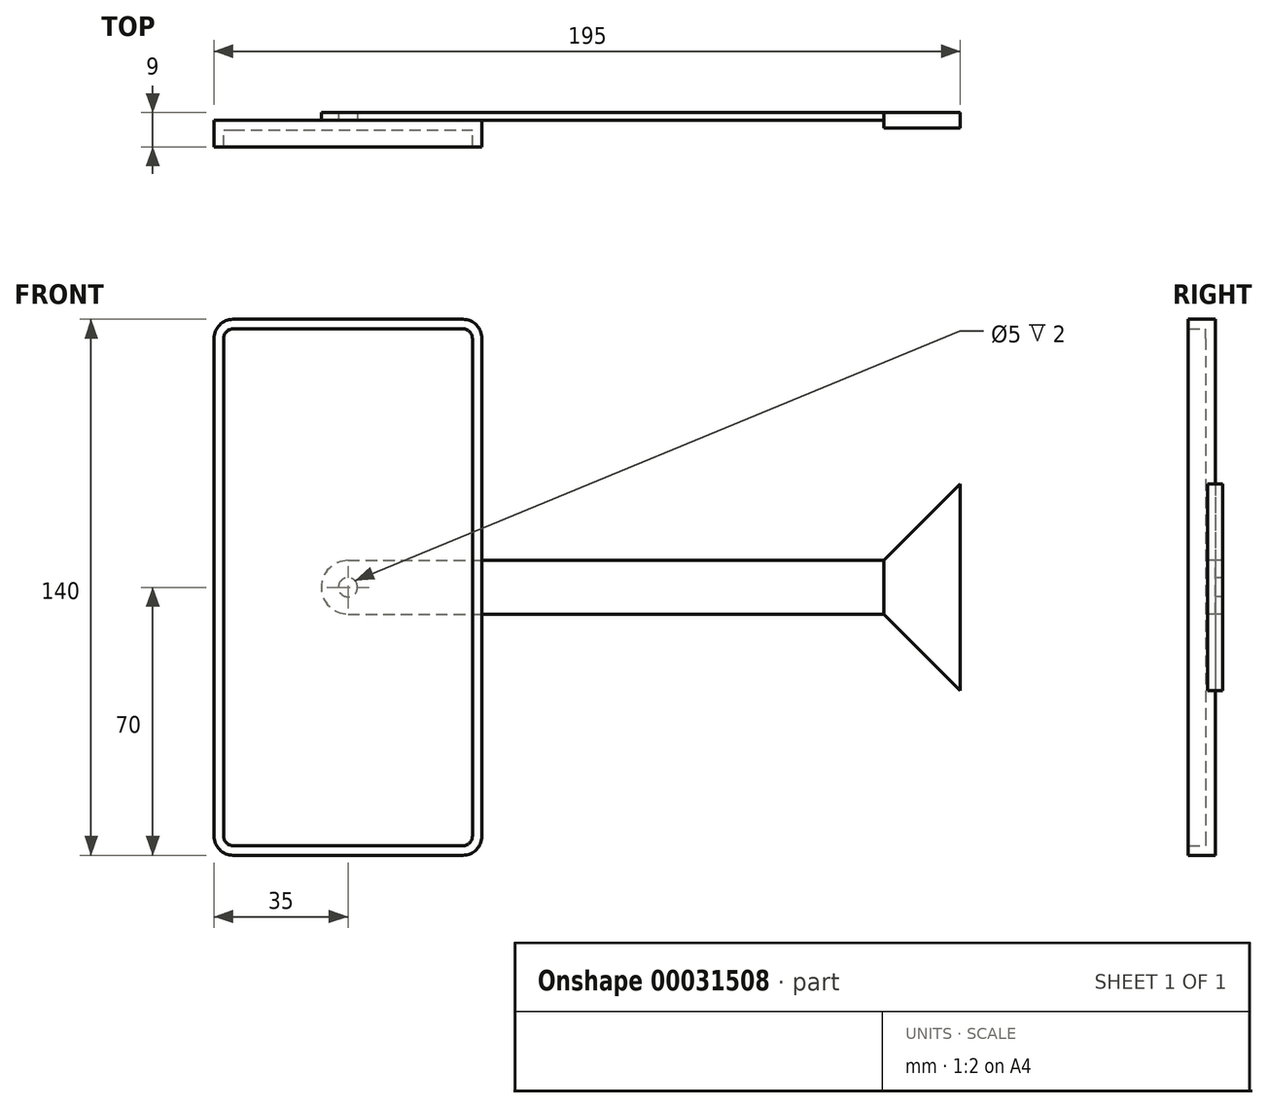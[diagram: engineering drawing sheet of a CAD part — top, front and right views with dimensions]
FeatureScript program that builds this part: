
annotation { "Feature Type Name" : "Feature", "Feature Type Description" : "" }
export const myFeature = defineFeature(function(context is Context, id is Id, definition is map)
    precondition{}
    {
        {
            var Q0;
            Q0=qCreatedBy(makeId("Front.planeOp"),FACE);
            var sketch = newSketch(context, id + "F0", { "sketchPlane" : qUnion([Q0])});
            skLineSegment(sketch, "E0.bottom", {"start": v(-35, 70) * mm, "end": v(35, 70) * mm});
            skLineSegment(sketch, "E0.top", {"start": v(-35, -70) * mm, "end": v(35, -70) * mm});
            skLineSegment(sketch, "E0.left", {"start": v(-35, 70) * mm, "end": v(-35, -70) * mm});
            skLineSegment(sketch, "E0.right", {"start": v(35, 70) * mm, "end": v(35, -70) * mm});
            skLineSegment(sketch, "E1", {"start": v(0, 0) * mm, "end": v(0, 56.64) * mm, "construction": true});
            skLineSegment(sketch, "E2", {"start": v(0, 0) * mm, "end": v(-68.66, 0) * mm, "construction": true});
            skSolve(sketch);
        }
        {
            var Q0;
            Q0=makeQuery(id+"F0.imprint","IMPRINT",FACE,{"disambiguationData":[TD([[makeQuery(id+"F0.imprint","IMPRINT",EDGE,{"derivedFrom":sQuery(id+"F0.wireOp",EDGE,"E0.bottom")}),-1.0]])]});
            extrude(context, id + "F1", {"entities" : qUnion([Q0]), "depth" : 7 * mm});
        }
        {
            var Q0;
            Q0=makeQuery(id+"F1.opExtrude","SWEPT_EDGE",EDGE,{"disambiguationData":[OSD([sQuery(id+"F0.wireOp",EDGE,"E0.bottom"),sQuery(id+"F0.wireOp",EDGE,"E0.right")])]});
            var Q1;
            Q1=makeQuery(id+"F1.opExtrude","SWEPT_EDGE",EDGE,{"disambiguationData":[OSD([sQuery(id+"F0.wireOp",EDGE,"E0.top"),sQuery(id+"F0.wireOp",EDGE,"E0.right")])]});
            var Q2;
            Q2=makeQuery(id+"F1.opExtrude","SWEPT_EDGE",EDGE,{"disambiguationData":[OSD([sQuery(id+"F0.wireOp",EDGE,"E0.top"),sQuery(id+"F0.wireOp",EDGE,"E0.left")])]});
            var Q3;
            Q3=makeQuery(id+"F1.opExtrude","SWEPT_EDGE",EDGE,{"disambiguationData":[OSD([sQuery(id+"F0.wireOp",EDGE,"E0.bottom"),sQuery(id+"F0.wireOp",EDGE,"E0.left")])]});
            fillet(context, id + "F2", {"entities" : qUnion([Q0, Q1, Q2, Q3]), "radius" : 5 * mm, "tangentPropagation" : true, "allowEdgeOverflow" : false});
        }
        {
            var Q0;
            Q0=makeQuery(id+"F1.opExtrude","CAP_FACE",FACE,{"disambiguationData":[OSD([sQuery(id+"F0.wireOp",EDGE,"E0.bottom"),sQuery(id+"F0.wireOp",EDGE,"E0.top"),sQuery(id+"F0.wireOp",EDGE,"E0.left"),sQuery(id+"F0.wireOp",EDGE,"E0.right")])],"isStart":false});
            shell(context, id + "F3", {"entities" : qUnion([Q0]), "thickness" : 2.5 * mm});
        }
        {
            var Q0;
            Q0=makeQuery(id+"F1.opExtrude","CAP_FACE",FACE,{"disambiguationData":[OSD([sQuery(id+"F0.wireOp",EDGE,"E0.bottom"),sQuery(id+"F0.wireOp",EDGE,"E0.top"),sQuery(id+"F0.wireOp",EDGE,"E0.left"),sQuery(id+"F0.wireOp",EDGE,"E0.right")])],"isStart":true});
            var sketch = newSketch(context, id + "F4", { "sketchPlane" : qUnion([Q0])});
            skLineSegment(sketch, "E3.bottom", {"start": v(0, -7) * mm, "end": v(-140, -7) * mm});
            skLineSegment(sketch, "E3.top", {"start": v(0, 7) * mm, "end": v(-140, 7) * mm});
            skLineSegment(sketch, "E3.right", {"start": v(-140, -7) * mm, "end": v(-140, 7) * mm});
            skLineSegment(sketch, "E4", {"start": v(0, 0) * mm, "end": v(45.25, 0) * mm, "construction": true});
            skArc(sketch, "E5", {"start": v(0, -7) * mm, "mid": v(7, 0) * mm, "end": v(0, 7) * mm});
            skCircle(sketch, "E6", {"center": v(0, 0) * mm, "radius": 2.5 * mm});
            skSolve(sketch);
        }
        {
            var Q0;
            {var subQ5=sQuery(id+"F4.wireOp",EDGE,"E3.right");Q0=makeQuery(id+"F4.imprint","IMPRINT",FACE,{"disambiguationData":[TD([[makeQuery(id+"F4.imprint","IMPRINT",EDGE,{"derivedFrom":subQ5}),-1.0]])]});}
            var Q1;
            {var subQ5=sQuery(id+"F4.wireOp",EDGE,"E5");Q1=makeQuery(id+"F4.imprint","IMPRINT",FACE,{"disambiguationData":[TD([[makeQuery(id+"F4.imprint","IMPRINT",EDGE,{"derivedFrom":subQ5}),1.0]])]});}
            extrude(context, id + "F5", {"entities" : qUnion([Q0, Q1]), "operationType" : NewBodyOperationType.ADD, "depth" : 2 * mm});
        }
        {
            var Q0;
            Q0=makeQuery(id+"F5.opExtrude","CAP_FACE",FACE,{"disambiguationData":[OSD([sQuery(id+"F4.wireOp",EDGE,"E3.bottom"),sQuery(id+"F4.wireOp",EDGE,"E3.top"),sQuery(id+"F4.wireOp",EDGE,"E3.right"),sQuery(id+"F4.wireOp",EDGE,"E5"),sQuery(id+"F4.wireOp",EDGE,"E6")])],"isStart":true});
            var sketch = newSketch(context, id + "F6", { "sketchPlane" : qUnion([Q0])});
            skLineSegment(sketch, "E7", {"start": v(140, 7) * mm, "end": v(160, 27) * mm});
            skLineSegment(sketch, "E8", {"start": v(160, 27) * mm, "end": v(160, -27) * mm});
            skLineSegment(sketch, "E9", {"start": v(160, -27) * mm, "end": v(140, -7) * mm});
            skLineSegment(sketch, "E10", {"start": v(140, 0) * mm, "end": v(170.5, 0) * mm, "construction": true});
            skSolve(sketch);
        }
        {
            var Q0;
            Q0=makeQuery(id+"F6.imprint","IMPRINT",FACE,{"disambiguationData":[TD([[makeQuery(id+"F6.imprint","IMPRINT",EDGE,{"derivedFrom":sQuery(id+"F6.wireOp",EDGE,"E7")}),-1.0]])]});
            extrude(context, id + "F7", {"entities" : qUnion([Q0]), "operationType" : NewBodyOperationType.ADD, "oppositeDirection" : true, "depth" : 2 * mm, "hasSecondDirection" : true, "secondDirectionOppositeDirection" : false, "secondDirectionDepth" : 2 * mm});
        }
    });
